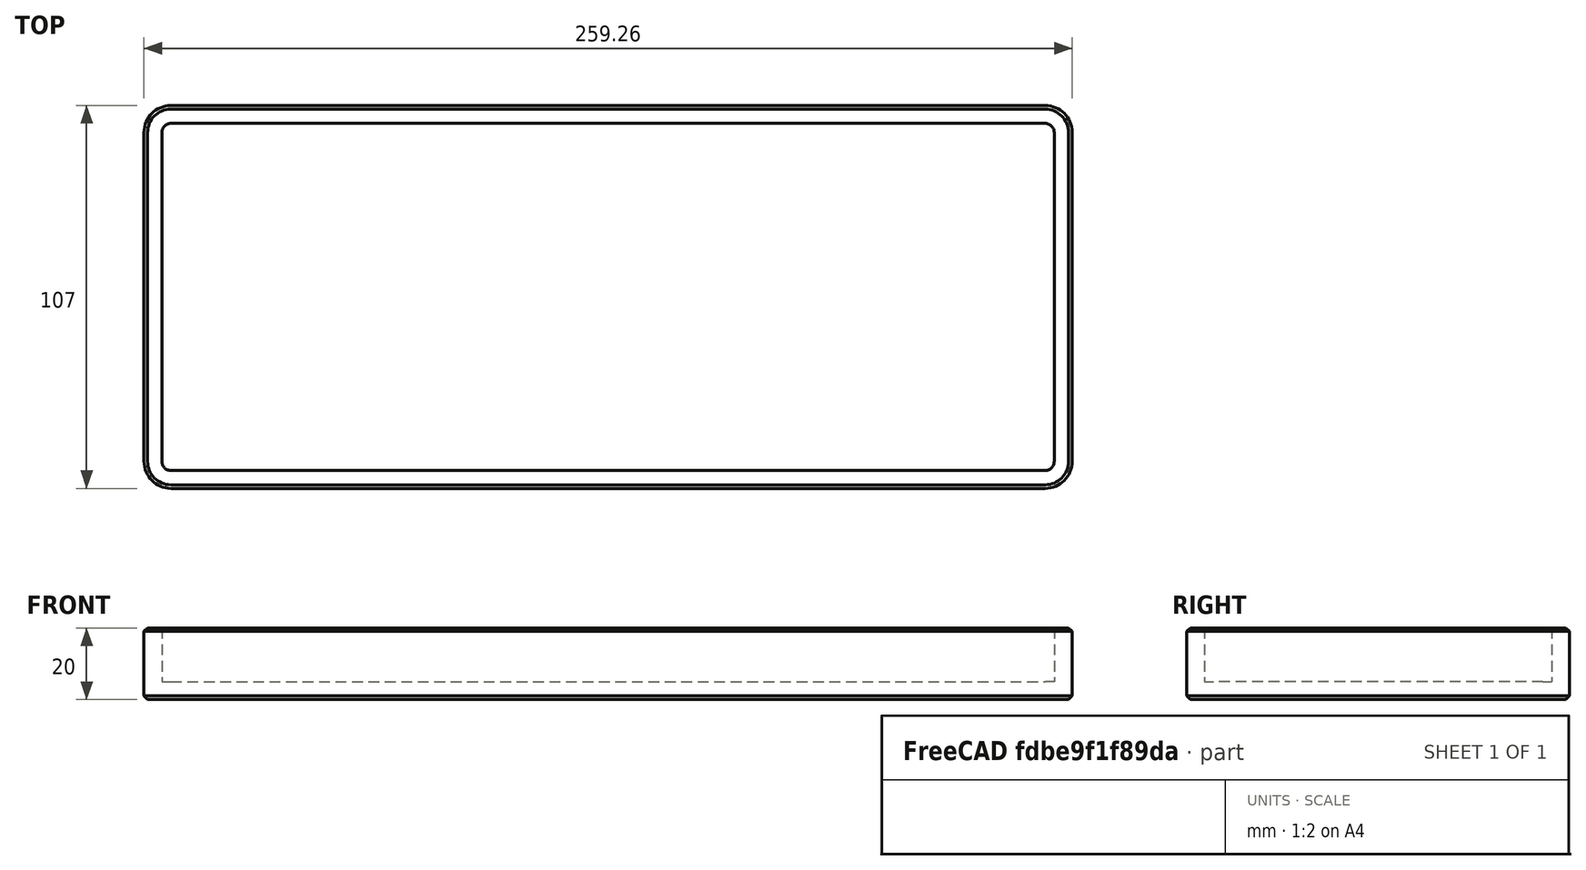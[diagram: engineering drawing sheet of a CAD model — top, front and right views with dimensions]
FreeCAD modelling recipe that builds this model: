
FCSTD DOCUMENT  (FreeCAD 0.19R24366 (Git))
Label: Keyboard
License: All rights reserved
LicenseURL: http://en.wikipedia.org/wiki/All_rights_reserved
objects: Sketcher::SketchObject×2, Spreadsheet::Sheet×1, PartDesign::Pad×1, PartDesign::Pocket×1, PartDesign::Chamfer×1, PartDesign::Body×1, Mesh::Feature×1
note: 9 computed .brp shape members not serialized (recipe doc carries the construction recipe); baked Part::Feature solids carry a one-line shape summary decoded from their .brp

FEATURE [Sketcher::SketchObject] Sketch
  FullyConstrained = true
  MapMode = 5
  Support = -> [XY_Plane]
  expr: Constraints[16] = Spreadsheet.Fillet
  expr: Constraints[19] = Spreadsheet.y
  expr: Constraints[14] = Spreadsheet.x
  expr: Constraints[17] = Spreadsheet.Fillet
  expr: Constraints[21] = Spreadsheet.x / 2
  expr: Constraints[18] = Spreadsheet.Fillet
  expr: Constraints[15] = Spreadsheet.Fillet
  expr: Constraints[20] = Spreadsheet.y / 2
  sketch-geometry (10):
    g0: GeomPoint X=0 Y=0 Z=0
    g1: LineSegment StartX=-129.63 StartY=-46 StartZ=0 EndX=-129.63 EndY=46 EndZ=0
    g2: LineSegment StartX=-122.13 StartY=53.5 StartZ=0 EndX=122.13 EndY=53.5 EndZ=0
    g3: LineSegment StartX=129.63 StartY=46 StartZ=0 EndX=129.63 EndY=-46 EndZ=0
    g4: LineSegment StartX=122.13 StartY=-53.5 StartZ=0 EndX=-122.13 EndY=-53.5 EndZ=0
    g5: GeomPoint X=0 Y=0 Z=0
    g6: ArcOfCircle CenterX=122.13 CenterY=46 CenterZ=0 NormalX=0 NormalY=0 NormalZ=1 AngleXU=0 Radius=7.5 StartAngle=0 EndAngle=1.5708
    g7: ArcOfCircle CenterX=-122.13 CenterY=46 CenterZ=0 NormalX=0 NormalY=0 NormalZ=1 AngleXU=0 Radius=7.5 StartAngle=1.5708 EndAngle=3.14159
    g8: ArcOfCircle CenterX=-122.13 CenterY=-46 CenterZ=0 NormalX=0 NormalY=0 NormalZ=1 AngleXU=0 Radius=7.5 StartAngle=3.14159 EndAngle=4.71239
    g9: ArcOfCircle CenterX=122.13 CenterY=-46 CenterZ=0 NormalX=0 NormalY=0 NormalZ=1 AngleXU=0 Radius=7.5 StartAngle=4.71239 EndAngle=6.28319
  constraints (22):
    c: Coincident(g0,g-1)
    c: Horizontal(g2)
    c: Horizontal(g4)
    c: Vertical(g1)
    c: Vertical(g3)
    c: Coincident(g5,g0)
    c: Tangent(g2,g6) = 1.5708
    c: Tangent(g3,g6) = 1.5708
    c: Tangent(g1,g7) = 1.5708
    c: Tangent(g2,g7) = 1.5708
    c: Tangent(g1,g8) = 1.5708
    c: Tangent(g4,g8) = 1.5708
    c: Tangent(g3,g9) = 1.5708
    c: Tangent(g4,g9) = 1.5708
    c: DistanceX(g1,g3) = 259.26
    c: Radius(g9) = 7.5
    c: Radius(g8) = 7.5
    c: Radius(g7) = 7.5
    c: Radius(g6) = 7.5
    c: DistanceY(g4,g2) = 107
    c: DistanceY(g0,g2) = 53.5
    c: DistanceX(g1,g0) = 129.63
FEATURE [Spreadsheet::Sheet] Spreadsheet
  cells = B2=x; C2(x)==254.26mm + C4; B3=y; C3(y)==107mm; B4=Thickness; C4(Thickness)==5mm; B5=Fillet; C5(Fillet)==7.5mm; B6=Edge Chamfer; C6(Edge)==1mm; B7=Height; C7(Height)==20mm
FEATURE [PartDesign::Pad] Pad
  Direction = (1,1,1)
  Length = 20
  Length2 = 100
  Profile = -> Sketch
  Refine = true
  Type = 0
  expr: Length = Spreadsheet.Height
FEATURE [Sketcher::SketchObject] Sketch001
  FullyConstrained = true
  MapMode = 5
  Placement = pos=(0,0,20) rot=(0,0,1;0rad)
  Support = -> [Pad]
  expr: Constraints[12] = Spreadsheet.y / 2 - Spreadsheet.Thickness
  expr: Constraints[13] = Spreadsheet.y / 2 - Spreadsheet.Thickness
  expr: Constraints[14] = Spreadsheet.x / 2 - Spreadsheet.Thickness
  expr: Constraints[17] = Spreadsheet.Fillet - Spreadsheet.Thickness
  expr: Constraints[15] = Spreadsheet.x / 2 - Spreadsheet.Thickness
  expr: Constraints[16] = Spreadsheet.Fillet - Spreadsheet.Thickness
  expr: Constraints[18] = Spreadsheet.Fillet - Spreadsheet.Thickness
  expr: Constraints[19] = Spreadsheet.Fillet - Spreadsheet.Thickness
  sketch-geometry (8):
    g0: LineSegment StartX=-122.13 StartY=48.5 StartZ=0 EndX=122.13 EndY=48.5 EndZ=0
    g1: LineSegment StartX=124.63 StartY=46 StartZ=0 EndX=124.63 EndY=-46 EndZ=0
    g2: LineSegment StartX=122.13 StartY=-48.5 StartZ=0 EndX=-122.13 EndY=-48.5 EndZ=0
    g3: LineSegment StartX=-124.63 StartY=-46 StartZ=0 EndX=-124.63 EndY=46 EndZ=0
    g4: ArcOfCircle CenterX=122.13 CenterY=46 CenterZ=0 NormalX=0 NormalY=0 NormalZ=1 AngleXU=0 Radius=2.5 StartAngle=1e-16 EndAngle=1.5708
    g5: ArcOfCircle CenterX=-122.13 CenterY=46 CenterZ=0 NormalX=0 NormalY=0 NormalZ=1 AngleXU=0 Radius=2.5 StartAngle=1.5708 EndAngle=3.14159
    g6: ArcOfCircle CenterX=-122.13 CenterY=-46 CenterZ=0 NormalX=0 NormalY=0 NormalZ=1 AngleXU=0 Radius=2.5 StartAngle=3.14159 EndAngle=4.71239
    g7: ArcOfCircle CenterX=122.13 CenterY=-46 CenterZ=0 NormalX=0 NormalY=0 NormalZ=1 AngleXU=0 Radius=2.5 StartAngle=4.71239 EndAngle=6.28319
  constraints (20):
    c: Horizontal(g0)
    c: Horizontal(g2)
    c: Vertical(g1)
    c: Vertical(g3)
    c: Tangent(g0,g4) = 1.5708
    c: Tangent(g1,g4) = 1.5708
    c: Tangent(g0,g5) = 1.5708
    c: Tangent(g3,g5) = 1.5708
    c: Tangent(g2,g6) = 1.5708
    c: Tangent(g3,g6) = 1.5708
    c: Tangent(g1,g7) = 1.5708
    c: Tangent(g2,g7) = 1.5708
    c: DistanceY(g-1,g0) = 48.5
    c: DistanceY(g2,g-1) = 48.5
    c: DistanceX(g-1,g1) = 124.63
    c: DistanceX(g3,g-1) = 124.63
    c: Radius(g4) = 2.5
    c: Radius(g7) = 2.5
    c: Radius(g5) = 2.5
    c: Radius(g6) = 2.5
FEATURE [PartDesign::Pocket] Pocket
  BaseFeature = -> Pad
  Length = 15
  Length2 = 100
  Profile = -> Sketch001
  Refine = true
  Type = 0
  expr: Length = Spreadsheet.Height - Spreadsheet.Thickness
FEATURE [PartDesign::Chamfer] Chamfer
  Angle = 45
  Base = -> Pocket [Edge20,Edge19,Edge17,Edge10,Edge4,Edge7,Edge16,Edge18,Edge14,Edge15,Edge6,Edge3,Edge9,Edge11,Edge12,Edge13]
  BaseFeature = -> Pocket
  ChamferType = 0
  FlipDirection = false
  Refine = true
  Size = 1
  Size2 = 1
  SupportTransform = false
  expr: Size = Spreadsheet.Edge
FEATURE [PartDesign::Body] Body
  Group = -> [Sketch,Pad,Sketch001,Pocket,Chamfer]
  Origin = -> Origin
  Tip = -> Chamfer
FEATURE [Mesh::Feature] OrthodoxLayout
  Placement = pos=(-114.25,38,12.25) rot=(0,0,1;0rad)
